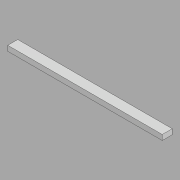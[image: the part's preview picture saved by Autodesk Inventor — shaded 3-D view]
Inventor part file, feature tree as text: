
AUTODESK INVENTOR PART (.ipt)
format: ipt  version: 2022.2 (Build 262287010, 287A)  size: 104,960 bytes
history: native  units: in
note: dims shown in document units (in); Inventor stores cm internally (conversion verified against a paired STEP export)
features: direct_edit x1, other x1, revolve x1
ambient origin geometry x8: Origin, YZ Plane, XZ Plane, XY Plane, X Axis, Y Axis, Z Axis, Center Point
bodies: Solid1 (feature_tree)
feature tree (3):
  direct_edit  "Direct Edit1"
  other  "Head (1) (1)"
  revolve  "Rotate1"  Angle=90.0deg
